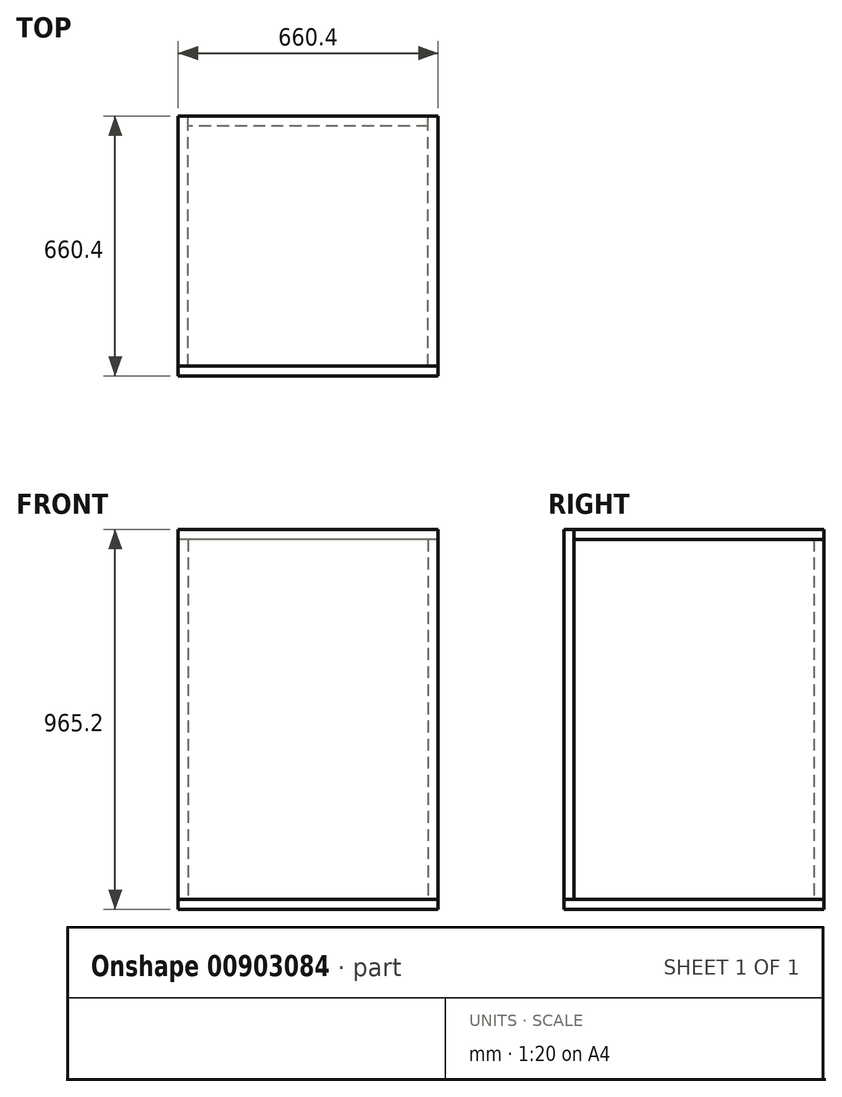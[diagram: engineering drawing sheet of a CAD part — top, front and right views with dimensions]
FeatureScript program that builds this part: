
annotation { "Feature Type Name" : "Feature", "Feature Type Description" : "" }
export const myFeature = defineFeature(function(context is Context, id is Id, definition is map)
    precondition{}
    {
        {
            var Q0;
            Q0=qCreatedBy(makeId("Top.planeOp"),FACE);
            var sketch = newSketch(context, id + "F0", { "sketchPlane" : qUnion([Q0])});
            skLineSegment(sketch, "E0.bottom", {"start": v(304.8, -304.8) * mm, "end": v(-304.8, -304.8) * mm});
            skLineSegment(sketch, "E0.top", {"start": v(304.8, 304.8) * mm, "end": v(-304.8, 304.8) * mm});
            skLineSegment(sketch, "E0.left", {"start": v(304.8, -304.8) * mm, "end": v(304.8, 304.8) * mm});
            skLineSegment(sketch, "E0.right", {"start": v(-304.8, -304.8) * mm, "end": v(-304.8, 304.8) * mm});
            skPoint(sketch, "E0.middle", {"position": v(0, 0) * mm});
            skLineSegment(sketch, "E1.bottom", {"start": v(330.2, -330.2) * mm, "end": v(-330.2, -330.2) * mm});
            skLineSegment(sketch, "E1.top", {"start": v(330.2, 330.2) * mm, "end": v(-330.2, 330.2) * mm});
            skLineSegment(sketch, "E1.left", {"start": v(330.2, -330.2) * mm, "end": v(330.2, 330.2) * mm});
            skLineSegment(sketch, "E1.right", {"start": v(-330.2, -330.2) * mm, "end": v(-330.2, 330.2) * mm});
            skLineSegment(sketch, "E2", {"start": v(-304.8, 304.8) * mm, "end": v(-304.8, 330.2) * mm});
            skLineSegment(sketch, "E3", {"start": v(304.8, 304.8) * mm, "end": v(304.8, 330.2) * mm});
            skLineSegment(sketch, "E4", {"start": v(-304.8, -304.8) * mm, "end": v(-330.2, -304.8) * mm});
            skLineSegment(sketch, "E5", {"start": v(304.8, -304.8) * mm, "end": v(330.2, -304.8) * mm});
            skSolve(sketch);
        }
        {
            var Q0;
            Q0=makeQuery(id+"F0.imprint","IMPRINT",FACE,{"disambiguationData":[TD([[makeQuery(id+"F0.imprint","IMPRINT",EDGE,{"derivedFrom":sQuery(id+"F0.wireOp",EDGE,"E0.right")}),1.0]])]});
            var Q1;
            Q1=makeQuery(id+"F0.imprint","IMPRINT",FACE,{"disambiguationData":[TD([[makeQuery(id+"F0.imprint","IMPRINT",EDGE,{"derivedFrom":sQuery(id+"F0.wireOp",EDGE,"E0.left")}),-1.0]])]});
            extrude(context, id + "F1", {"entities" : qUnion([Q0, Q1]), "depth" : 914.4 * mm, "offsetDistance" : 25.4 * mm});
        }
        {
            var Q0;
            Q0=makeQuery(id+"F0.imprint","IMPRINT",FACE,{"disambiguationData":[TD([[makeQuery(id+"F0.imprint","IMPRINT",EDGE,{"derivedFrom":sQuery(id+"F0.wireOp",EDGE,"E0.top")}),-1.0]])]});
            var Q1;
            Q1=makeQuery(id+"F1.opExtrude","CAP_FACE",FACE,{"disambiguationData":[OSD([sQuery(id+"F0.wireOp",EDGE,"E0.right"),sQuery(id+"F0.wireOp",EDGE,"E1.top"),sQuery(id+"F0.wireOp",EDGE,"E1.right"),sQuery(id+"F0.wireOp",EDGE,"E2"),sQuery(id+"F0.wireOp",EDGE,"E4")])],"isStart":false});
            extrude(context, id + "F2", {"entities" : qUnion([Q0]), "endBound" : BoundingType.UP_TO_SURFACE, "depth" : 25.4 * mm, "endBoundEntityFace" : qUnion([Q1]), "offsetDistance" : 25.4 * mm});
        }
        {
            var Q0;
            Q0=makeQuery(id+"F1.opExtrude","CAP_FACE",FACE,{"disambiguationData":[OSD([sQuery(id+"F0.wireOp",EDGE,"E0.right"),sQuery(id+"F0.wireOp",EDGE,"E1.top"),sQuery(id+"F0.wireOp",EDGE,"E1.right"),sQuery(id+"F0.wireOp",EDGE,"E2"),sQuery(id+"F0.wireOp",EDGE,"E4")])],"isStart":false});
            var sketch = newSketch(context, id + "F3", { "sketchPlane" : qUnion([Q0])});
            skLineSegment(sketch, "E6.0", {"start": v(-330.2, -304.8) * mm, "end": v(-330.2, 330.2) * mm});
            skLineSegment(sketch, "E6.2", {"start": v(330.2, -304.8) * mm, "end": v(330.2, 330.2) * mm});
            skLineSegment(sketch, "E6.3", {"start": v(330.2, 330.2) * mm, "end": v(-330.2, 330.2) * mm});
            skLineSegment(sketch, "E7", {"start": v(-330.2, -304.8) * mm, "end": v(330.2, -304.8) * mm});
            skPoint(sketch, "E6.1.end.orphan", {"position": v(-330.2, -330.2) * mm});
            skPoint(sketch, "E6.1.start.orphan", {"position": v(330.2, -330.2) * mm});
            skSolve(sketch);
        }
        {
            var Q0;
            Q0 = qSketchRegion(id + "F3", true);
            extrude(context, id + "F4", {"entities" : qUnion([Q0]), "depth" : 25.4 * mm, "offsetDistance" : 25.4 * mm});
        }
        {
            var Q0;
            Q0=qCreatedBy(makeId("Top.planeOp"),FACE);
            var sketch = newSketch(context, id + "F5", { "sketchPlane" : qUnion([Q0])});
            skLineSegment(sketch, "E8.0", {"start": v(-330.2, -330.2) * mm, "end": v(-330.2, 330.2) * mm});
            skLineSegment(sketch, "E8.1", {"start": v(330.2, -330.2) * mm, "end": v(330.2, 330.2) * mm});
            skLineSegment(sketch, "E8.2", {"start": v(330.2, 330.2) * mm, "end": v(-330.2, 330.2) * mm});
            skPoint(sketch, "E8.4", {"position": v(-330.2, -330.2) * mm});
            skPoint(sketch, "E8.5", {"position": v(-330.2, -330.2) * mm});
            skPoint(sketch, "E8.6", {"position": v(330.2, -330.2) * mm});
            skPoint(sketch, "E8.7", {"position": v(330.2, -330.2) * mm});
            skLineSegment(sketch, "E9.0", {"start": v(330.2, -330.2) * mm, "end": v(-330.2, -330.2) * mm});
            skSolve(sketch);
        }
        {
            var Q0;
            Q0 = qSketchRegion(id + "F5", true);
            extrude(context, id + "F6", {"entities" : qUnion([Q0]), "oppositeDirection" : true, "depth" : 25.4 * mm, "offsetDistance" : 25.4 * mm});
        }
        {
            var Q0;
            Q0=makeQuery(id+"F1.opExtrude","SWEPT_FACE",FACE,{"disambiguationData":[OSD([sQuery(id+"F0.wireOp",EDGE,"E4")])]});
            var sketch = newSketch(context, id + "F7", { "sketchPlane" : qUnion([Q0])});
            skLineSegment(sketch, "E10.bottom", {"start": v(-330.2, 939.8) * mm, "end": v(330.2, 939.8) * mm});
            skLineSegment(sketch, "E10.top", {"start": v(-330.2, 0) * mm, "end": v(330.2, 0) * mm});
            skLineSegment(sketch, "E10.left", {"start": v(-330.2, 939.8) * mm, "end": v(-330.2, 0) * mm});
            skLineSegment(sketch, "E10.right", {"start": v(330.2, 939.8) * mm, "end": v(330.2, 0) * mm});
            skSolve(sketch);
        }
        {
            var Q0;
            Q0 = qSketchRegion(id + "F7", true);
            extrude(context, id + "F8", {"entities" : qUnion([Q0]), "depth" : 25.4 * mm, "offsetDistance" : 25.4 * mm});
        }
    });
